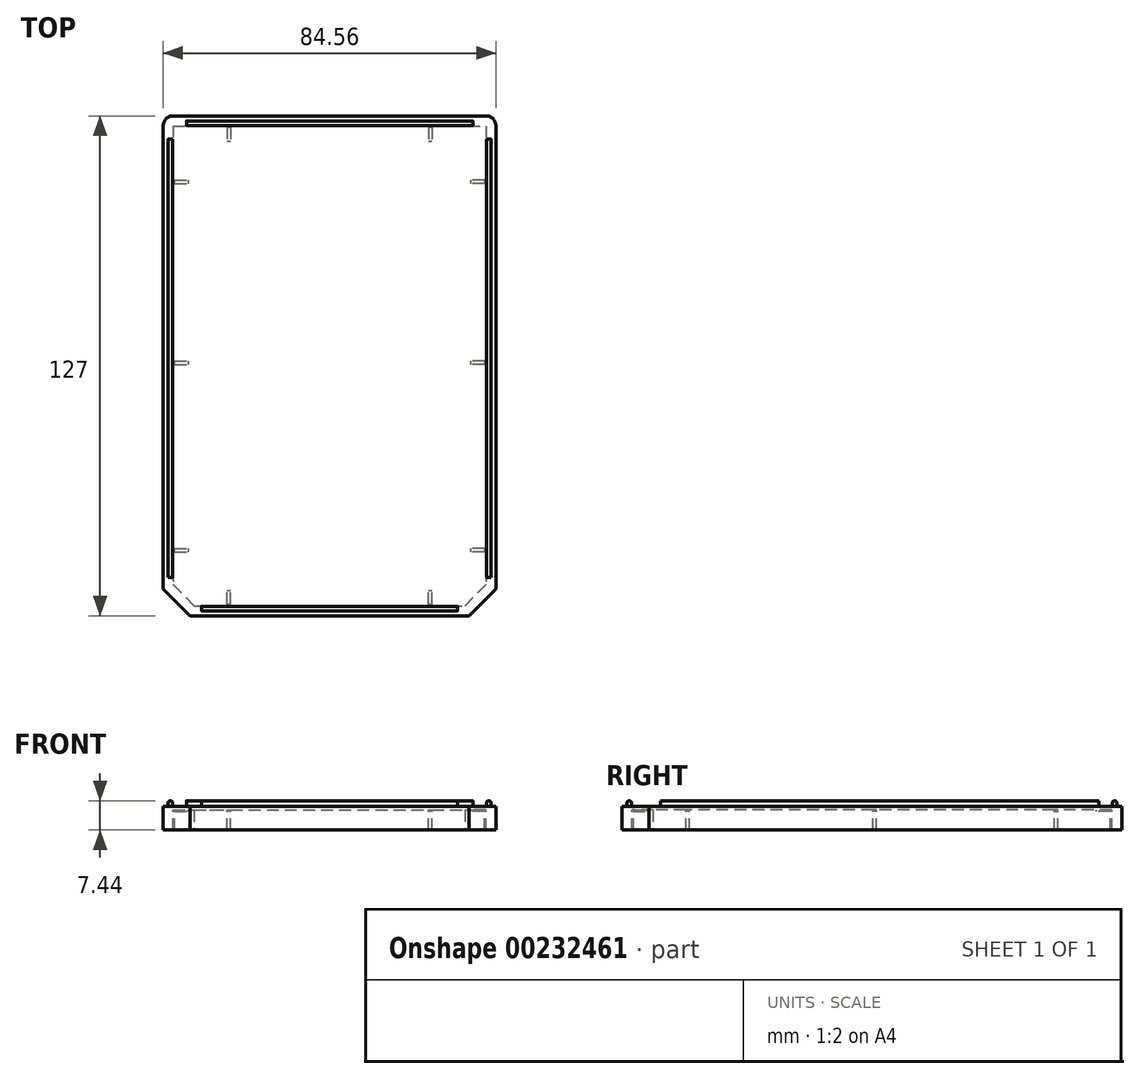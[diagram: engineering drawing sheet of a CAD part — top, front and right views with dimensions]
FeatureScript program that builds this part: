
annotation { "Feature Type Name" : "Feature", "Feature Type Description" : "" }
export const myFeature = defineFeature(function(context is Context, id is Id, definition is map)
    precondition{}
    {
        {
            var Q0;
            Q0=qCreatedBy(makeId("Top.planeOp"),FACE);
            var sketch = newSketch(context, id + "F0", { "sketchPlane" : qUnion([Q0])});
            skLineSegment(sketch, "E0.bottom", {"start": v(-42.28, 63.5) * mm, "end": v(42.28, 63.5) * mm});
            skLineSegment(sketch, "E0.top", {"start": v(-35.42, -63.5) * mm, "end": v(35.42, -63.5) * mm});
            skLineSegment(sketch, "E0.left", {"start": v(-42.28, 63.5) * mm, "end": v(-42.28, -56.64) * mm});
            skLineSegment(sketch, "E0.right", {"start": v(42.28, 63.5) * mm, "end": v(42.28, -56.64) * mm});
            skLineSegment(sketch, "E1", {"start": v(-42.28, -56.64) * mm, "end": v(-35.42, -63.5) * mm});
            skLineSegment(sketch, "E2", {"start": v(35.42, -63.5) * mm, "end": v(42.28, -56.64) * mm});
            skSolve(sketch);
        }
        {
            var Q0;
            Q0=makeQuery(id+"F0.imprint","IMPRINT",FACE,{"disambiguationData":[TD([[makeQuery(id+"F0.imprint","IMPRINT",EDGE,{"derivedFrom":sQuery(id+"F0.wireOp",EDGE,"E0.bottom")}),-1.0]])]});
            extrude(context, id + "F1", {"entities" : qUnion([Q0]), "depth" : 6.02 * mm});
        }
        {
            var Q0;
            Q0=makeQuery(id+"F1.opExtrude","SWEPT_EDGE",EDGE,{"disambiguationData":[OSD([sQuery(id+"F0.wireOp",EDGE,"E0.bottom"),sQuery(id+"F0.wireOp",EDGE,"E0.left")])]});
            var Q1;
            Q1=makeQuery(id+"F1.opExtrude","SWEPT_EDGE",EDGE,{"disambiguationData":[OSD([sQuery(id+"F0.wireOp",EDGE,"E0.bottom"),sQuery(id+"F0.wireOp",EDGE,"E0.right")])]});
            fillet(context, id + "F2", {"entities" : qUnion([Q0, Q1]), "radius" : 2.54 * mm, "tangentPropagation" : true, "allowEdgeOverflow" : false});
        }
        {
            var Q0;
            Q0=makeQuery(id+"F1.opExtrude","CAP_FACE",FACE,{"disambiguationData":[OSD([sQuery(id+"F0.wireOp",EDGE,"E0.bottom"),sQuery(id+"F0.wireOp",EDGE,"E0.top"),sQuery(id+"F0.wireOp",EDGE,"E0.left"),sQuery(id+"F0.wireOp",EDGE,"E0.right"),sQuery(id+"F0.wireOp",EDGE,"E1"),sQuery(id+"F0.wireOp",EDGE,"E2")])],"isStart":true});
            var sketch = newSketch(context, id + "F3", { "sketchPlane" : qUnion([Q0])});
            skLineSegment(sketch, "E3.0", {"start": v(-39.74, -60.96) * mm, "end": v(39.74, -60.96) * mm});
            skLineSegment(sketch, "E4.0", {"start": v(39.74, -60.96) * mm, "end": v(39.74, 55.59) * mm});
            skLineSegment(sketch, "E5.0", {"start": v(-39.74, -60.96) * mm, "end": v(-39.74, 55.59) * mm});
            skLineSegment(sketch, "E6.0", {"start": v(-34.37, 60.96) * mm, "end": v(34.37, 60.96) * mm});
            skLineSegment(sketch, "E7.0", {"start": v(-39.74, 55.59) * mm, "end": v(-34.37, 60.96) * mm});
            skLineSegment(sketch, "E8.0", {"start": v(34.37, 60.96) * mm, "end": v(39.74, 55.59) * mm});
            skSolve(sketch);
        }
        {
            var Q0;
            Q0 = qSketchRegion(id + "F3", true);
            extrude(context, id + "F4", {"entities" : qUnion([Q0]), "operationType" : NewBodyOperationType.REMOVE, "oppositeDirection" : true, "depth" : 5.08 * mm});
        }
        {
            var Q0;
            Q0=makeQuery(id+"F4.boolean.opBoolean","COPY",FACE,{"derivedFrom":makeQuery(id+"F4.opExtrude","CAP_FACE",FACE,{"disambiguationData":[OSD([sQuery(id+"F3.wireOp",EDGE,"E3.0"),sQuery(id+"F3.wireOp",EDGE,"E4.0"),sQuery(id+"F3.wireOp",EDGE,"E5.0"),sQuery(id+"F3.wireOp",EDGE,"E6.0"),sQuery(id+"F3.wireOp",EDGE,"E7.0"),sQuery(id+"F3.wireOp",EDGE,"E8.0")])],"isStart":false})});
            var sketch = newSketch(context, id + "F5", { "sketchPlane" : qUnion([Q0])});
            skLineSegment(sketch, "E9.bottom", {"start": v(39.74, 47.24) * mm, "end": v(35.88, 47.24) * mm});
            skLineSegment(sketch, "E9.top", {"start": v(39.74, 46.36) * mm, "end": v(35.88, 46.36) * mm});
            skLineSegment(sketch, "E9.left", {"start": v(39.74, 47.24) * mm, "end": v(39.74, 46.36) * mm});
            skLineSegment(sketch, "E9.right", {"start": v(35.88, 47.24) * mm, "end": v(35.88, 46.36) * mm});
            skLineSegment(sketch, "E10.bottom", {"start": v(39.74, -0.3) * mm, "end": v(35.88, -0.3) * mm});
            skLineSegment(sketch, "E10.top", {"start": v(39.74, -1.18) * mm, "end": v(35.88, -1.18) * mm});
            skLineSegment(sketch, "E10.left", {"start": v(39.74, -0.3) * mm, "end": v(39.74, -1.18) * mm});
            skLineSegment(sketch, "E10.right", {"start": v(35.88, -0.3) * mm, "end": v(35.88, -1.18) * mm});
            skLineSegment(sketch, "E11.bottom", {"start": v(39.74, -46.35) * mm, "end": v(35.88, -46.35) * mm});
            skLineSegment(sketch, "E11.top", {"start": v(39.74, -47.24) * mm, "end": v(35.88, -47.24) * mm});
            skLineSegment(sketch, "E11.left", {"start": v(39.74, -46.35) * mm, "end": v(39.74, -47.24) * mm});
            skLineSegment(sketch, "E11.right", {"start": v(35.88, -46.35) * mm, "end": v(35.88, -47.24) * mm});
            skLineSegment(sketch, "E12.bottom", {"start": v(25.13, -60.96) * mm, "end": v(26.02, -60.96) * mm});
            skLineSegment(sketch, "E12.top", {"start": v(25.13, -57.1) * mm, "end": v(26.02, -57.1) * mm});
            skLineSegment(sketch, "E12.left", {"start": v(25.13, -60.96) * mm, "end": v(25.13, -57.1) * mm});
            skLineSegment(sketch, "E12.right", {"start": v(26.02, -60.96) * mm, "end": v(26.02, -57.1) * mm});
            skLineSegment(sketch, "E13.bottom", {"start": v(-26.02, -60.96) * mm, "end": v(-25.13, -60.96) * mm});
            skLineSegment(sketch, "E13.top", {"start": v(-26.02, -57.1) * mm, "end": v(-25.13, -57.1) * mm});
            skLineSegment(sketch, "E13.left", {"start": v(-26.02, -60.96) * mm, "end": v(-26.02, -57.1) * mm});
            skLineSegment(sketch, "E13.right", {"start": v(-25.13, -60.96) * mm, "end": v(-25.13, -57.1) * mm});
            skLineSegment(sketch, "E14.bottom", {"start": v(-39.74, -47.24) * mm, "end": v(-35.88, -47.24) * mm});
            skLineSegment(sketch, "E14.top", {"start": v(-39.74, -46.35) * mm, "end": v(-35.88, -46.35) * mm});
            skLineSegment(sketch, "E14.left", {"start": v(-39.74, -47.24) * mm, "end": v(-39.74, -46.35) * mm});
            skLineSegment(sketch, "E14.right", {"start": v(-35.88, -47.24) * mm, "end": v(-35.88, -46.35) * mm});
            skLineSegment(sketch, "E15.bottom", {"start": v(-39.74, -1.18) * mm, "end": v(-35.88, -1.18) * mm});
            skLineSegment(sketch, "E15.top", {"start": v(-39.74, -0.3) * mm, "end": v(-35.88, -0.3) * mm});
            skLineSegment(sketch, "E15.left", {"start": v(-39.74, -1.18) * mm, "end": v(-39.74, -0.3) * mm});
            skLineSegment(sketch, "E15.right", {"start": v(-35.88, -1.18) * mm, "end": v(-35.88, -0.3) * mm});
            skLineSegment(sketch, "E16.bottom", {"start": v(-39.74, 46.36) * mm, "end": v(-35.88, 46.36) * mm});
            skLineSegment(sketch, "E16.top", {"start": v(-39.74, 47.24) * mm, "end": v(-35.88, 47.24) * mm});
            skLineSegment(sketch, "E16.left", {"start": v(-39.74, 46.36) * mm, "end": v(-39.74, 47.24) * mm});
            skLineSegment(sketch, "E16.right", {"start": v(-35.88, 46.36) * mm, "end": v(-35.88, 47.24) * mm});
            skLineSegment(sketch, "E17.bottom", {"start": v(-26.02, 60.96) * mm, "end": v(-25.13, 60.96) * mm});
            skLineSegment(sketch, "E17.top", {"start": v(-26.02, 57.1) * mm, "end": v(-25.13, 57.1) * mm});
            skLineSegment(sketch, "E17.left", {"start": v(-26.02, 60.96) * mm, "end": v(-26.02, 57.1) * mm});
            skLineSegment(sketch, "E17.right", {"start": v(-25.13, 60.96) * mm, "end": v(-25.13, 57.1) * mm});
            skLineSegment(sketch, "E18.bottom", {"start": v(25.13, 60.96) * mm, "end": v(26.02, 60.96) * mm});
            skLineSegment(sketch, "E18.top", {"start": v(25.13, 57.1) * mm, "end": v(26.02, 57.1) * mm});
            skLineSegment(sketch, "E18.left", {"start": v(25.13, 60.96) * mm, "end": v(25.13, 57.1) * mm});
            skLineSegment(sketch, "E18.right", {"start": v(26.02, 60.96) * mm, "end": v(26.02, 57.1) * mm});
            skSolve(sketch);
        }
        {
            var Q0;
            Q0 = qSketchRegion(id + "F5", true);
            extrude(context, id + "F6", {"entities" : qUnion([Q0]), "operationType" : NewBodyOperationType.ADD, "depth" : 0.36 * mm});
        }
        {
            var Q0;
            Q0=makeQuery(id+"F4.boolean.opBoolean","COPY",FACE,{"derivedFrom":makeQuery(id+"F4.opExtrude","CAP_FACE",FACE,{"disambiguationData":[OSD([sQuery(id+"F3.wireOp",EDGE,"E3.0"),sQuery(id+"F3.wireOp",EDGE,"E4.0"),sQuery(id+"F3.wireOp",EDGE,"E5.0"),sQuery(id+"F3.wireOp",EDGE,"E6.0"),sQuery(id+"F3.wireOp",EDGE,"E7.0"),sQuery(id+"F3.wireOp",EDGE,"E8.0")])],"isStart":false})});
            var sketch = newSketch(context, id + "F7", { "sketchPlane" : qUnion([Q0])});
            skLineSegment(sketch, "E19.bottom", {"start": v(-26.02, 60.96) * mm, "end": v(-25.13, 60.96) * mm});
            skLineSegment(sketch, "E19.top", {"start": v(-26.02, 60.6) * mm, "end": v(-25.13, 60.6) * mm});
            skLineSegment(sketch, "E19.left", {"start": v(-26.02, 60.96) * mm, "end": v(-26.02, 60.6) * mm});
            skLineSegment(sketch, "E19.right", {"start": v(-25.13, 60.96) * mm, "end": v(-25.13, 60.6) * mm});
            skLineSegment(sketch, "E20.bottom", {"start": v(25.13, 60.96) * mm, "end": v(26.02, 60.96) * mm});
            skLineSegment(sketch, "E20.top", {"start": v(25.13, 60.6) * mm, "end": v(26.02, 60.6) * mm});
            skLineSegment(sketch, "E20.left", {"start": v(25.13, 60.96) * mm, "end": v(25.13, 60.6) * mm});
            skLineSegment(sketch, "E20.right", {"start": v(26.02, 60.96) * mm, "end": v(26.02, 60.6) * mm});
            skLineSegment(sketch, "E21.bottom", {"start": v(39.74, 47.24) * mm, "end": v(39.38, 47.24) * mm});
            skLineSegment(sketch, "E21.top", {"start": v(39.74, 46.36) * mm, "end": v(39.38, 46.36) * mm});
            skLineSegment(sketch, "E21.left", {"start": v(39.74, 47.24) * mm, "end": v(39.74, 46.36) * mm});
            skLineSegment(sketch, "E21.right", {"start": v(39.38, 47.24) * mm, "end": v(39.38, 46.36) * mm});
            skLineSegment(sketch, "E22.bottom", {"start": v(39.38, -0.3) * mm, "end": v(39.74, -0.3) * mm});
            skLineSegment(sketch, "E22.top", {"start": v(39.38, -1.18) * mm, "end": v(39.74, -1.18) * mm});
            skLineSegment(sketch, "E22.left", {"start": v(39.38, -0.3) * mm, "end": v(39.38, -1.18) * mm});
            skLineSegment(sketch, "E22.right", {"start": v(39.74, -0.3) * mm, "end": v(39.74, -1.18) * mm});
            skLineSegment(sketch, "E23.bottom", {"start": v(-39.74, 47.24) * mm, "end": v(-39.38, 47.24) * mm});
            skLineSegment(sketch, "E23.top", {"start": v(-39.74, 46.36) * mm, "end": v(-39.38, 46.36) * mm});
            skLineSegment(sketch, "E23.left", {"start": v(-39.74, 47.24) * mm, "end": v(-39.74, 46.36) * mm});
            skLineSegment(sketch, "E23.right", {"start": v(-39.38, 47.24) * mm, "end": v(-39.38, 46.36) * mm});
            skLineSegment(sketch, "E24.bottom", {"start": v(-39.74, -0.3) * mm, "end": v(-39.38, -0.3) * mm});
            skLineSegment(sketch, "E24.top", {"start": v(-39.74, -1.18) * mm, "end": v(-39.38, -1.18) * mm});
            skLineSegment(sketch, "E24.left", {"start": v(-39.74, -0.3) * mm, "end": v(-39.74, -1.18) * mm});
            skLineSegment(sketch, "E24.right", {"start": v(-39.38, -0.3) * mm, "end": v(-39.38, -1.18) * mm});
            skLineSegment(sketch, "E25.bottom", {"start": v(-39.74, -46.35) * mm, "end": v(-39.38, -46.35) * mm});
            skLineSegment(sketch, "E25.top", {"start": v(-39.74, -47.24) * mm, "end": v(-39.38, -47.24) * mm});
            skLineSegment(sketch, "E25.left", {"start": v(-39.74, -46.35) * mm, "end": v(-39.74, -47.24) * mm});
            skLineSegment(sketch, "E25.right", {"start": v(-39.38, -46.35) * mm, "end": v(-39.38, -47.24) * mm});
            skLineSegment(sketch, "E26.bottom", {"start": v(-26.02, -60.96) * mm, "end": v(-25.13, -60.96) * mm});
            skLineSegment(sketch, "E26.top", {"start": v(-26.02, -60.6) * mm, "end": v(-25.13, -60.6) * mm});
            skLineSegment(sketch, "E26.left", {"start": v(-26.02, -60.96) * mm, "end": v(-26.02, -60.6) * mm});
            skLineSegment(sketch, "E26.right", {"start": v(-25.13, -60.96) * mm, "end": v(-25.13, -60.6) * mm});
            skLineSegment(sketch, "E27.bottom", {"start": v(25.13, -60.96) * mm, "end": v(26.02, -60.96) * mm});
            skLineSegment(sketch, "E27.top", {"start": v(25.13, -60.6) * mm, "end": v(26.02, -60.6) * mm});
            skLineSegment(sketch, "E27.left", {"start": v(25.13, -60.96) * mm, "end": v(25.13, -60.6) * mm});
            skLineSegment(sketch, "E27.right", {"start": v(26.02, -60.96) * mm, "end": v(26.02, -60.6) * mm});
            skLineSegment(sketch, "E28.bottom", {"start": v(39.74, -47.24) * mm, "end": v(39.38, -47.24) * mm});
            skLineSegment(sketch, "E28.top", {"start": v(39.74, -46.35) * mm, "end": v(39.38, -46.35) * mm});
            skLineSegment(sketch, "E28.left", {"start": v(39.74, -47.24) * mm, "end": v(39.74, -46.35) * mm});
            skLineSegment(sketch, "E28.right", {"start": v(39.38, -47.24) * mm, "end": v(39.38, -46.35) * mm});
            skSolve(sketch);
        }
        {
            var Q0;
            Q0 = qSketchRegion(id + "F7", true);
            extrude(context, id + "F8", {"entities" : qUnion([Q0]), "operationType" : NewBodyOperationType.ADD, "depth" : 5.08 * mm});
        }
        {
            var Q0;
            Q0=makeQuery(id+"F1.opExtrude","CAP_FACE",FACE,{"disambiguationData":[OSD([sQuery(id+"F0.wireOp",EDGE,"E0.bottom"),sQuery(id+"F0.wireOp",EDGE,"E0.top"),sQuery(id+"F0.wireOp",EDGE,"E0.left"),sQuery(id+"F0.wireOp",EDGE,"E0.right"),sQuery(id+"F0.wireOp",EDGE,"E1"),sQuery(id+"F0.wireOp",EDGE,"E2")])],"isStart":false});
            var sketch = newSketch(context, id + "F9", { "sketchPlane" : qUnion([Q0])});
            skLineSegment(sketch, "E29.bottom", {"start": v(-41, 57.6) * mm, "end": v(-39.87, 57.6) * mm});
            skLineSegment(sketch, "E29.top", {"start": v(-41, -53.77) * mm, "end": v(-39.87, -53.77) * mm});
            skLineSegment(sketch, "E29.left", {"start": v(-41, 57.6) * mm, "end": v(-41, -53.77) * mm});
            skLineSegment(sketch, "E29.right", {"start": v(-39.87, 57.6) * mm, "end": v(-39.87, -53.77) * mm});
            skLineSegment(sketch, "E30.bottom", {"start": v(-32.55, -61.09) * mm, "end": v(32.55, -61.09) * mm});
            skLineSegment(sketch, "E30.top", {"start": v(-32.55, -62.23) * mm, "end": v(32.55, -62.23) * mm});
            skLineSegment(sketch, "E30.left", {"start": v(-32.55, -61.09) * mm, "end": v(-32.55, -62.23) * mm});
            skLineSegment(sketch, "E30.right", {"start": v(32.55, -61.09) * mm, "end": v(32.55, -62.23) * mm});
            skLineSegment(sketch, "E31.bottom", {"start": v(41, -53.77) * mm, "end": v(39.87, -53.77) * mm});
            skLineSegment(sketch, "E31.top", {"start": v(41, 57.6) * mm, "end": v(39.87, 57.6) * mm});
            skLineSegment(sketch, "E31.left", {"start": v(41, -53.77) * mm, "end": v(41, 57.6) * mm});
            skLineSegment(sketch, "E31.right", {"start": v(39.87, -53.77) * mm, "end": v(39.87, 57.6) * mm});
            skLineSegment(sketch, "E32.bottom", {"start": v(-36.39, 62.23) * mm, "end": v(36.39, 62.23) * mm});
            skLineSegment(sketch, "E32.top", {"start": v(-36.39, 61.09) * mm, "end": v(36.39, 61.09) * mm});
            skLineSegment(sketch, "E32.left", {"start": v(-36.39, 62.23) * mm, "end": v(-36.39, 61.09) * mm});
            skLineSegment(sketch, "E32.right", {"start": v(36.39, 62.23) * mm, "end": v(36.39, 61.09) * mm});
            skSolve(sketch);
        }
        {
            var Q0;
            Q0 = qSketchRegion(id + "F9", true);
            extrude(context, id + "F10", {"entities" : qUnion([Q0]), "operationType" : NewBodyOperationType.ADD, "depth" : 1.42 * mm});
        }
        {
            var Q0;
            Q0=makeQuery(id+"F10.opExtrude","CAP_EDGE",EDGE,{"disambiguationData":[OSD([sQuery(id+"F9.wireOp",EDGE,"E29.left")])],"isStart":false});
            var Q1;
            Q1=makeQuery(id+"F10.opExtrude","CAP_EDGE",EDGE,{"disambiguationData":[OSD([sQuery(id+"F9.wireOp",EDGE,"E29.right")])],"isStart":false});
            var Q2;
            Q2=makeQuery(id+"F10.opExtrude","CAP_EDGE",EDGE,{"disambiguationData":[OSD([sQuery(id+"F9.wireOp",EDGE,"E32.top")])],"isStart":false});
            var Q3;
            Q3=makeQuery(id+"F10.opExtrude","CAP_EDGE",EDGE,{"disambiguationData":[OSD([sQuery(id+"F9.wireOp",EDGE,"E32.bottom")])],"isStart":false});
            var Q4;
            Q4=makeQuery(id+"F10.opExtrude","CAP_EDGE",EDGE,{"disambiguationData":[OSD([sQuery(id+"F9.wireOp",EDGE,"E31.right")])],"isStart":false});
            var Q5;
            Q5=makeQuery(id+"F10.opExtrude","CAP_EDGE",EDGE,{"disambiguationData":[OSD([sQuery(id+"F9.wireOp",EDGE,"E31.left")])],"isStart":false});
            var Q6;
            Q6=makeQuery(id+"F10.opExtrude","CAP_EDGE",EDGE,{"disambiguationData":[OSD([sQuery(id+"F9.wireOp",EDGE,"E30.bottom")])],"isStart":false});
            var Q7;
            Q7=makeQuery(id+"F10.opExtrude","CAP_EDGE",EDGE,{"disambiguationData":[OSD([sQuery(id+"F9.wireOp",EDGE,"E30.top")])],"isStart":false});
            fillet(context, id + "F11", {"entities" : qUnion([Q0, Q1, Q2, Q3, Q4, Q5, Q6, Q7]), "radius" : 0.5 * mm, "tangentPropagation" : true, "allowEdgeOverflow" : false});
        }
    });
